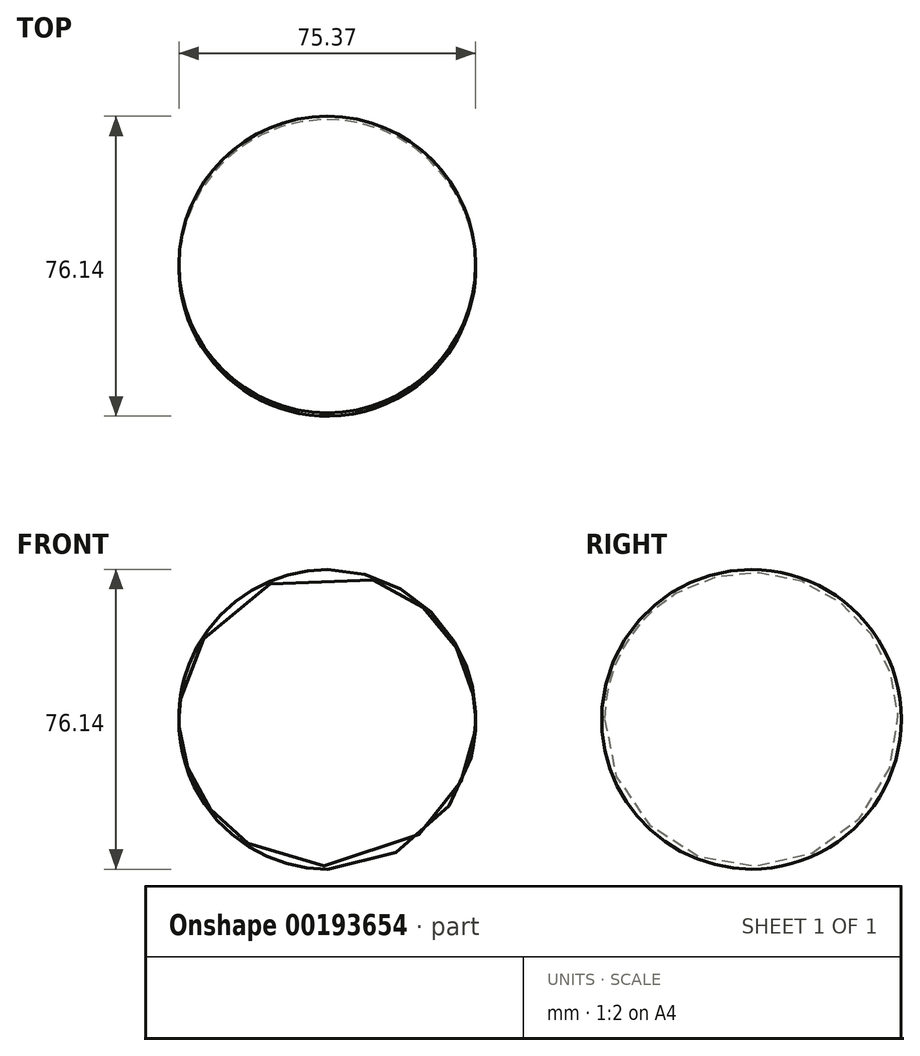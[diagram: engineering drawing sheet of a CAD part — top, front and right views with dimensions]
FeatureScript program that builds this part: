
annotation { "Feature Type Name" : "Feature", "Feature Type Description" : "" }
export const myFeature = defineFeature(function(context is Context, id is Id, definition is map)
    precondition{}
    {
        {
            var Q0;
            Q0=qCreatedBy(makeId("Top.planeOp"),FACE);
            var sketch = newSketch(context, id + "F0", { "sketchPlane" : qUnion([Q0])});
            skArc(sketch, "E0", {"start": v(37.67, 0.94) * mm, "mid": v(-0.54, 37.67) * mm, "end": v(-37.68, -0.15) * mm});
            skLineSegment(sketch, "E1", {"start": v(37.67, 0.94) * mm, "end": v(-37.68, -0.15) * mm});
            skSolve(sketch);
        }
        {
            var Q0;
            Q0=makeQuery(id+"F0.imprint","IMPRINT",FACE,{"disambiguationData":[TD([[makeQuery(id+"F0.imprint","IMPRINT",EDGE,{"derivedFrom":sQuery(id+"F0.wireOp",EDGE,"E0")}),1.0]])]});
            var Q1;
            Q1=sQuery(id+"F0.wireOp",EDGE,"E1");
            revolve(context, id + "F1", {"entities" : qUnion([Q0]), "axis" : qUnion([Q1]), "revolveType" : RevolveType.FULL});
        }
    });
